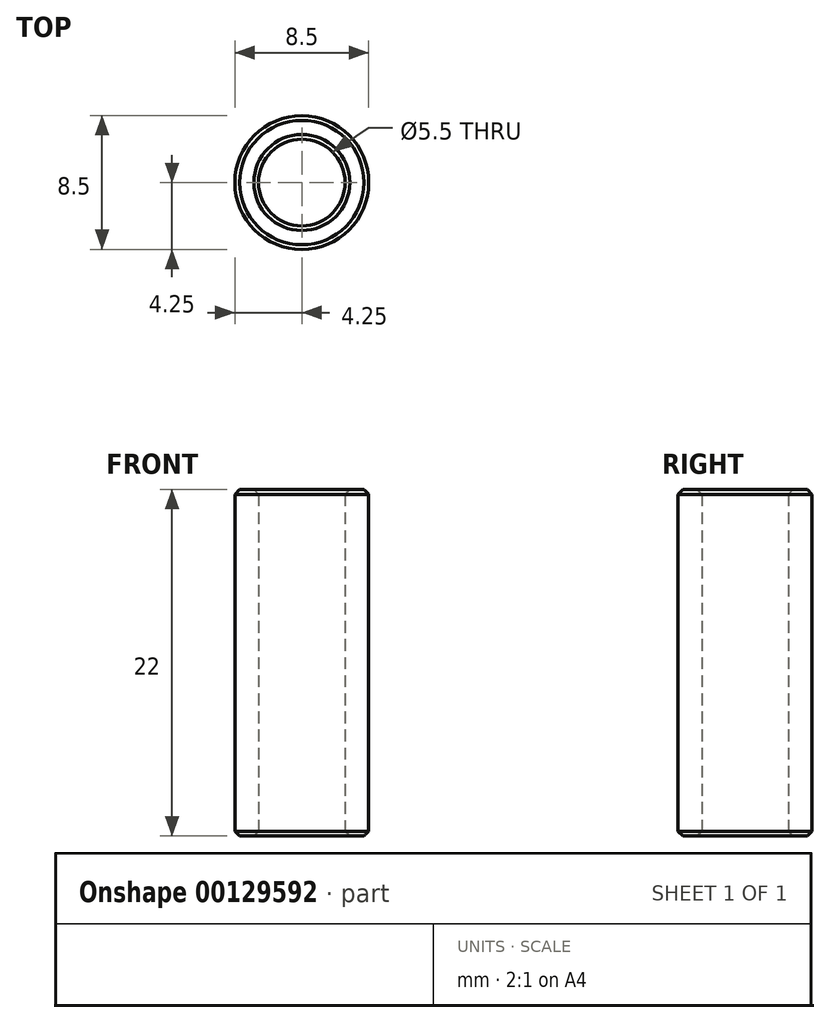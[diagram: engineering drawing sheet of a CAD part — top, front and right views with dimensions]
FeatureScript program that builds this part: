
annotation { "Feature Type Name" : "Feature", "Feature Type Description" : "" }
export const myFeature = defineFeature(function(context is Context, id is Id, definition is map)
    precondition{}
    {
        {
            var Q0;
            Q0=qCreatedBy(makeId("Top.planeOp"),FACE);
            var sketch = newSketch(context, id + "F0", { "sketchPlane" : qUnion([Q0])});
            skCircle(sketch, "E0", {"center": v(0, 0) * mm, "radius": 4.25 * mm});
            skCircle(sketch, "E1", {"center": v(0, 0) * mm, "radius": 2.75 * mm});
            skSolve(sketch);
        }
        {
            var Q0;
            Q0 = qSketchRegion(id + "F0", true);
            extrude(context, id + "F1", {"entities" : qUnion([Q0]), "depth" : 22 * mm});
        }
        {
            var Q0;
            Q0=makeQuery(id+"F1.opExtrude","CAP_EDGE",EDGE,{"disambiguationData":[OSD([sQuery(id+"F0.wireOp",EDGE,"E1")])],"isStart":false});
            var Q1;
            Q1=makeQuery(id+"F1.opExtrude","CAP_EDGE",EDGE,{"disambiguationData":[OSD([sQuery(id+"F0.wireOp",EDGE,"E1")])],"isStart":true});
            var Q2;
            Q2=makeQuery(id+"F1.opExtrude","CAP_EDGE",EDGE,{"disambiguationData":[OSD([sQuery(id+"F0.wireOp",EDGE,"E0")])],"isStart":false});
            var Q3;
            Q3=makeQuery(id+"F1.opExtrude","CAP_EDGE",EDGE,{"disambiguationData":[OSD([sQuery(id+"F0.wireOp",EDGE,"E0")])],"isStart":true});
            chamfer(context, id + "F2", {"entities" : qUnion([Q0, Q1, Q2, Q3]), "width" : .3 * mm, "tangentPropagation" : true});
        }
    });
